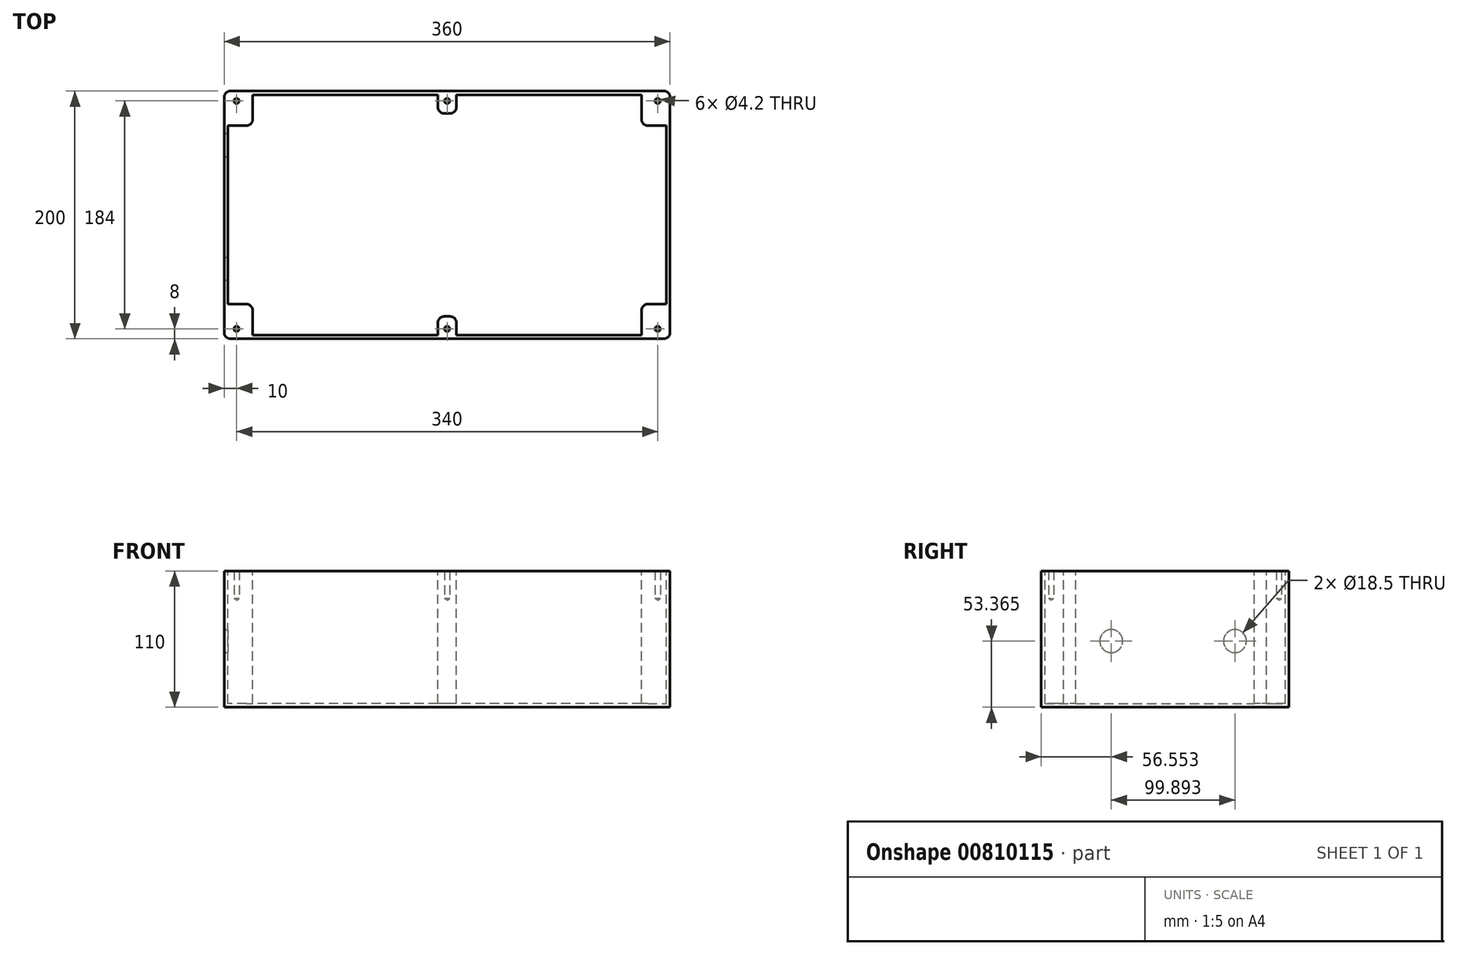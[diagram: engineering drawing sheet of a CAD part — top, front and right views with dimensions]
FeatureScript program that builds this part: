
annotation { "Feature Type Name" : "Feature", "Feature Type Description" : "" }
export const myFeature = defineFeature(function(context is Context, id is Id, definition is map)
    precondition{}
    {
        {
            var Q0;
            Q0=qCreatedBy(makeId("Top.planeOp"),FACE);
            var sketch = newSketch(context, id + "F0", { "sketchPlane" : qUnion([Q0])});
            skLineSegment(sketch, "E0.bottom", {"start": v(180, -100) * mm, "end": v(-180, -100) * mm});
            skLineSegment(sketch, "E0.top", {"start": v(180, 100) * mm, "end": v(-180, 100) * mm});
            skLineSegment(sketch, "E0.left", {"start": v(180, -100) * mm, "end": v(180, 100) * mm});
            skLineSegment(sketch, "E0.right", {"start": v(-180, -100) * mm, "end": v(-180, 100) * mm});
            skPoint(sketch, "E0.middle", {"position": v(0, 0) * mm});
            skSolve(sketch);
        }
        {
            var Q0;
            Q0=makeQuery(id+"F0.imprint","IMPRINT",FACE,{"disambiguationData":[TD([[makeQuery(id+"F0.imprint","IMPRINT",EDGE,{"derivedFrom":sQuery(id+"F0.wireOp",EDGE,"E0.bottom")}),-1.0]])]});
            extrude(context, id + "F1", {"entities" : qUnion([Q0]), "depth" : 110 * mm, "offsetDistance" : 25 * mm});
        }
        {
            var Q0;
            Q0=makeQuery(id+"F1.opExtrude","SWEPT_EDGE",EDGE,{"disambiguationData":[OSD([sQuery(id+"F0.wireOp",EDGE,"E0.top"),sQuery(id+"F0.wireOp",EDGE,"E0.right")])]});
            var Q1;
            Q1=makeQuery(id+"F1.opExtrude","SWEPT_EDGE",EDGE,{"disambiguationData":[OSD([sQuery(id+"F0.wireOp",EDGE,"E0.bottom"),sQuery(id+"F0.wireOp",EDGE,"E0.right")])]});
            var Q2;
            Q2=makeQuery(id+"F1.opExtrude","SWEPT_EDGE",EDGE,{"disambiguationData":[OSD([sQuery(id+"F0.wireOp",EDGE,"E0.bottom"),sQuery(id+"F0.wireOp",EDGE,"E0.left")])]});
            var Q3;
            Q3=makeQuery(id+"F1.opExtrude","SWEPT_EDGE",EDGE,{"disambiguationData":[OSD([sQuery(id+"F0.wireOp",EDGE,"E0.top"),sQuery(id+"F0.wireOp",EDGE,"E0.left")])]});
            fillet(context, id + "F2", {"entities" : qUnion([Q0, Q1, Q2, Q3]), "radius" : 5 * mm, "tangentPropagation" : true, "allowEdgeOverflow" : false});
        }
        {
            var Q0;
            Q0=makeQuery(id+"F1.opExtrude","CAP_FACE",FACE,{"disambiguationData":[OSD([sQuery(id+"F0.wireOp",EDGE,"E0.bottom"),sQuery(id+"F0.wireOp",EDGE,"E0.top"),sQuery(id+"F0.wireOp",EDGE,"E0.left"),sQuery(id+"F0.wireOp",EDGE,"E0.right")])],"isStart":false});
            shell(context, id + "F3", {"entities" : qUnion([Q0]), "thickness" : 3 * mm});
        }
        {
            var Q0;
            Q0=makeQuery(id+"F1.opExtrude","SWEPT_FACE",FACE,{"disambiguationData":[OSD([sQuery(id+"F0.wireOp",EDGE,"E0.right")])]});
            var sketch = newSketch(context, id + "F4", { "sketchPlane" : qUnion([Q0])});
            skPoint(sketch, "E1", {"position": v(-56.45, 53.37) * mm});
            skPoint(sketch, "E2", {"position": v(43.45, 53.37) * mm});
            skSolve(sketch);
        }
        {
            var Q0;
            Q0=sQuery(id+"F4.wireOp",VERTEX,"E1");
            var Q1;
            Q1=sQuery(id+"F4.wireOp",VERTEX,"E2");
            var Q2;
            Q2=makeQuery(id+"F1.opExtrude","SWEPT_BODY",BODY,{"disambiguationData":[OSD([sQuery(id+"F0.wireOp",EDGE,"E0.bottom"),sQuery(id+"F0.wireOp",EDGE,"E0.top"),sQuery(id+"F0.wireOp",EDGE,"E0.left"),sQuery(id+"F0.wireOp",EDGE,"E0.right")])]});
            hole(context, id + "F5", {"style" : HoleStyle.SIMPLE, "endStyle" : HoleEndStyle.BLIND, "standardTappedOrClearance" : lookupTablePath({ "standard" : "ISO", "engagement" : "75%", "pitch" : "1.5 mm", "size" : "M20", "type" : "Tapped" }), "standardBlindInLast" : lookupTablePath({ "standard" : "ISO", "fit" : "Normal", "engagement" : "75%", "pitch" : "1.5 mm", "size" : "M20", "type" : "Clearance & tapped" }), "holeDiameter" : 18.5 * mm, "majorDiameter" : 20 * mm, "showTappedDepth" : true, "holeDepth" : 16.5 * mm, "isTappedThrough" : true, "tappedDepth" : 12 * mm, "tapClearance" : 3, "locations" : qUnion([Q0, Q1]), "scope" : qUnion([Q2])});
        }
        {
            var Q0;
            Q0=makeQuery(id+"F1.opExtrude","CAP_FACE",FACE,{"disambiguationData":[OSD([sQuery(id+"F0.wireOp",EDGE,"E0.bottom"),sQuery(id+"F0.wireOp",EDGE,"E0.top"),sQuery(id+"F0.wireOp",EDGE,"E0.left"),sQuery(id+"F0.wireOp",EDGE,"E0.right")])],"isStart":false});
            var sketch = newSketch(context, id + "F6", { "sketchPlane" : qUnion([Q0])});
            skPoint(sketch, "E3", {"position": v(0, 92) * mm});
            skPoint(sketch, "E4", {"position": v(170, 92) * mm});
            skLineSegment(sketch, "E5", {"start": v(-210.1, 0) * mm, "end": v(238.92, 0) * mm, "construction": true});
            skPoint(sketch, "E5.startSnap0", {"position": v(-180, 0) * mm});
            skLineSegment(sketch, "E6", {"start": v(0, 133.37) * mm, "end": v(0, -145.7) * mm, "construction": true});
            skPoint(sketch, "E7.MirrorP", {"position": v(-170, 92) * mm});
            skPoint(sketch, "E8.MirrorP", {"position": v(0, -92) * mm});
            skPoint(sketch, "E9.MirrorP", {"position": v(170, -92) * mm});
            skPoint(sketch, "E10.MirrorP", {"position": v(-170, -92) * mm});
            skSolve(sketch);
        }
        {
            var Q0;
            {var subQ3=sQuery(id+"F0.wireOp",EDGE,"E0.bottom");var subQ10=makeQuery(id+"F1.opExtrude","CAP_EDGE",EDGE,{"disambiguationData":[OSD([subQ3])],"isStart":false});Q0=makeQuery(id+"F6.imprint","IMPRINT",FACE,{"disambiguationData":[TD([[makeQuery(id+"F6.imprint","IMPRINT",EDGE,{"derivedFrom":subQ10}),-1.0]])]});}
            var sketch = newSketch(context, id + "F7", { "sketchPlane" : qUnion([Q0])});
            skArc(sketch, "E11.0.0", {"start": v(175, -97) * mm, "mid": v(176.41, -96.41) * mm, "end": v(177, -95) * mm});
            skLineSegment(sketch, "E11.0.1", {"start": v(177, -95) * mm, "end": v(177, -72) * mm});
            skArc(sketch, "E11.0.2", {"start": v(177, 95) * mm, "mid": v(176.41, 96.41) * mm, "end": v(175, 97) * mm});
            skLineSegment(sketch, "E11.0.3", {"start": v(175, 97) * mm, "end": v(157, 97) * mm});
            skArc(sketch, "E11.0.4", {"start": v(-175, 97) * mm, "mid": v(-176.41, 96.41) * mm, "end": v(-177, 95) * mm});
            skLineSegment(sketch, "E11.0.5", {"start": v(-177, 95) * mm, "end": v(-177, 72) * mm});
            skArc(sketch, "E11.0.6", {"start": v(-177, -95) * mm, "mid": v(-176.41, -96.41) * mm, "end": v(-175, -97) * mm});
            skLineSegment(sketch, "E11.0.7", {"start": v(-175, -97) * mm, "end": v(-157, -97) * mm});
            skLineSegment(sketch, "E12.bottom", {"start": v(-177, 72) * mm, "end": v(-162, 72) * mm});
            skLineSegment(sketch, "E12.top", {"start": v(-177, 97) * mm, "end": v(-157, 97) * mm});
            skLineSegment(sketch, "E12.left", {"start": v(-177, 72) * mm, "end": v(-177, 97) * mm});
            skLineSegment(sketch, "E12.right", {"start": v(-157, 77) * mm, "end": v(-157, 97) * mm});
            skPoint(sketch, "E13.visualSharp", {"position": v(-157, 72) * mm});
            skArc(sketch, "E13.filletArc", {"start": v(-162, 72) * mm, "mid": v(-158.46, 73.46) * mm, "end": v(-157, 77) * mm});
            skLineSegment(sketch, "E14.bottom", {"start": v(177, 72) * mm, "end": v(162, 72) * mm});
            skLineSegment(sketch, "E14.top", {"start": v(177, 97) * mm, "end": v(157, 97) * mm});
            skLineSegment(sketch, "E14.left", {"start": v(177, 72) * mm, "end": v(177, 97) * mm});
            skLineSegment(sketch, "E14.right", {"start": v(157, 77) * mm, "end": v(157, 97) * mm});
            skPoint(sketch, "E15.visualSharp", {"position": v(157, 72) * mm});
            skArc(sketch, "E15.filletArc", {"start": v(157, 77) * mm, "mid": v(158.46, 73.46) * mm, "end": v(162, 72) * mm});
            skLineSegment(sketch, "E16.MirrorCS", {"start": v(177, -72) * mm, "end": v(162, -72) * mm});
            skArc(sketch, "E17.MirrorCS", {"start": v(157, -77) * mm, "mid": v(158.46, -73.46) * mm, "end": v(162, -72) * mm});
            skLineSegment(sketch, "E18.MirrorCS", {"start": v(157, -77) * mm, "end": v(157, -97) * mm});
            skLineSegment(sketch, "E19.MirrorCS", {"start": v(-177, -72) * mm, "end": v(-162, -72) * mm});
            skArc(sketch, "E20.MirrorCS", {"start": v(-162, -72) * mm, "mid": v(-158.46, -73.46) * mm, "end": v(-157, -77) * mm});
            skLineSegment(sketch, "E21.MirrorCS", {"start": v(-157, -77) * mm, "end": v(-157, -97) * mm});
            skLineSegment(sketch, "E22.bottom", {"start": v(-7.5, 97) * mm, "end": v(7.5, 97) * mm});
            skLineSegment(sketch, "E22.top", {"start": v(-2.5, 82) * mm, "end": v(2.5, 82) * mm});
            skLineSegment(sketch, "E22.left", {"start": v(-7.5, 97) * mm, "end": v(-7.5, 87) * mm});
            skLineSegment(sketch, "E22.right", {"start": v(7.5, 97) * mm, "end": v(7.5, 87) * mm});
            skPoint(sketch, "E23.visualSharp", {"position": v(-7.5, 82) * mm});
            skArc(sketch, "E23.filletArc", {"start": v(-7.5, 87) * mm, "mid": v(-6.04, 83.46) * mm, "end": v(-2.5, 82) * mm});
            skPoint(sketch, "E24.visualSharp", {"position": v(7.5, 82) * mm});
            skArc(sketch, "E24.filletArc", {"start": v(2.5, 82) * mm, "mid": v(6.04, 83.46) * mm, "end": v(7.5, 87) * mm});
            skLineSegment(sketch, "E25.MirrorCS", {"start": v(7.5, -97) * mm, "end": v(7.5, -87) * mm});
            skLineSegment(sketch, "E26.MirrorCS", {"start": v(-7.5, -97) * mm, "end": v(-7.5, -87) * mm});
            skArc(sketch, "E27.MirrorCS", {"start": v(-7.5, -87) * mm, "mid": v(-6.04, -83.46) * mm, "end": v(-2.5, -82) * mm});
            skLineSegment(sketch, "E28.MirrorCS", {"start": v(-2.5, -82) * mm, "end": v(2.5, -82) * mm});
            skArc(sketch, "E29.MirrorCS", {"start": v(2.5, -82) * mm, "mid": v(6.04, -83.46) * mm, "end": v(7.5, -87) * mm});
            skLineSegment(sketch, "E30.trimOffspring", {"start": v(-157, 97) * mm, "end": v(-175, 97) * mm});
            skLineSegment(sketch, "E31.trimOffspring", {"start": v(-177, -72) * mm, "end": v(-177, -95) * mm});
            skLineSegment(sketch, "E32.trimOffspring", {"start": v(-7.5, -97) * mm, "end": v(7.5, -97) * mm});
            skLineSegment(sketch, "E33.trimOffspring", {"start": v(157, -97) * mm, "end": v(175, -97) * mm});
            skLineSegment(sketch, "E34.trimOffspring", {"start": v(177, 72) * mm, "end": v(177, 95) * mm});
            skLineSegment(sketch, "E35.trimOffspring", {"start": v(7.5, 97) * mm, "end": v(-7.5, 97) * mm});
            skSolve(sketch);
        }
        {
            var Q0;
            {var subQ1=sQuery(id+"F7.wireOp",EDGE,"E11.0.4");Q0=makeQuery(id+"F7.imprint","IMPRINT",FACE,{"disambiguationData":[TD([[makeQuery(id+"F7.imprint","IMPRINT",EDGE,{"derivedFrom":subQ1}),1.0]])]});}
            var Q1;
            Q1=makeQuery(id+"F7.imprint","IMPRINT",FACE,{"disambiguationData":[TD([[makeQuery(id+"F7.imprint","IMPRINT",EDGE,{"derivedFrom":sQuery(id+"F7.wireOp",EDGE,"E11.0.6")}),1.0]])]});
            var Q2;
            Q2=makeQuery(id+"F7.imprint","IMPRINT",FACE,{"disambiguationData":[TD([[makeQuery(id+"F7.imprint","IMPRINT",EDGE,{"derivedFrom":sQuery(id+"F7.wireOp",EDGE,"E22.top")}),1.0]])]});
            var Q3;
            Q3=makeQuery(id+"F7.imprint","IMPRINT",FACE,{"disambiguationData":[TD([[makeQuery(id+"F7.imprint","IMPRINT",EDGE,{"derivedFrom":sQuery(id+"F7.wireOp",EDGE,"E25.MirrorCS")}),1.0]])]});
            var Q4;
            Q4=makeQuery(id+"F7.imprint","IMPRINT",FACE,{"disambiguationData":[TD([[makeQuery(id+"F7.imprint","IMPRINT",EDGE,{"derivedFrom":sQuery(id+"F7.wireOp",EDGE,"E11.0.0")}),1.0]])]});
            var Q5;
            {var subQ2=sQuery(id+"F7.wireOp",EDGE,"E11.0.2");Q5=makeQuery(id+"F7.imprint","IMPRINT",FACE,{"disambiguationData":[TD([[makeQuery(id+"F7.imprint","IMPRINT",EDGE,{"derivedFrom":subQ2}),1.0]])]});}
            var Q6;
            Q6=makeQuery(id+"F3.opShell","OFFSET_FACE",FACE,{"disambiguationData":[OSD([sQuery(id+"F0.wireOp",EDGE,"E0.bottom"),sQuery(id+"F0.wireOp",EDGE,"E0.top"),sQuery(id+"F0.wireOp",EDGE,"E0.left"),sQuery(id+"F0.wireOp",EDGE,"E0.right")])]});
            extrude(context, id + "F8", {"entities" : qUnion([Q0, Q1, Q2, Q3, Q4, Q5]), "operationType" : NewBodyOperationType.ADD, "endBound" : BoundingType.UP_TO_SURFACE, "oppositeDirection" : true, "depth" : 15 * mm, "endBoundEntityFace" : qUnion([Q6]), "offsetDistance" : 25 * mm});
        }
        {
            var Q0;
            Q0=sQuery(id+"F6.wireOp",VERTEX,"E10.MirrorP");
            var Q1;
            Q1=sQuery(id+"F6.wireOp",VERTEX,"E7.MirrorP");
            var Q2;
            Q2=sQuery(id+"F6.wireOp",VERTEX,"E3");
            var Q3;
            Q3=sQuery(id+"F6.wireOp",VERTEX,"E4");
            var Q4;
            Q4=sQuery(id+"F6.wireOp",VERTEX,"E9.MirrorP");
            var Q5;
            Q5=sQuery(id+"F6.wireOp",VERTEX,"E8.MirrorP");
            var Q6;
            Q6=makeQuery(id+"F1.opExtrude","SWEPT_BODY",BODY,{"disambiguationData":[OSD([sQuery(id+"F0.wireOp",EDGE,"E0.bottom"),sQuery(id+"F0.wireOp",EDGE,"E0.top"),sQuery(id+"F0.wireOp",EDGE,"E0.left"),sQuery(id+"F0.wireOp",EDGE,"E0.right")])]});
            hole(context, id + "F9", {"style" : HoleStyle.SIMPLE, "endStyle" : HoleEndStyle.BLIND, "standardTappedOrClearance" : lookupTablePath({ "standard" : "ISO", "engagement" : "75%", "pitch" : "0.8 mm", "size" : "M5", "type" : "Tapped" }), "standardBlindInLast" : lookupTablePath({ "standard" : "ISO", "engagement" : "75%", "pitch" : "0.8 mm", "size" : "M5", "type" : "Tapped" }), "holeDiameter" : 4.2 * mm, "majorDiameter" : 5 * mm, "showTappedDepth" : true, "holeDepth" : 22.4 * mm, "isTappedThrough" : true, "tappedDepth" : 20 * mm, "tapClearance" : 3, "locations" : qUnion([Q0, Q1, Q2, Q3, Q4, Q5]), "scope" : qUnion([Q6])});
        }
    });
